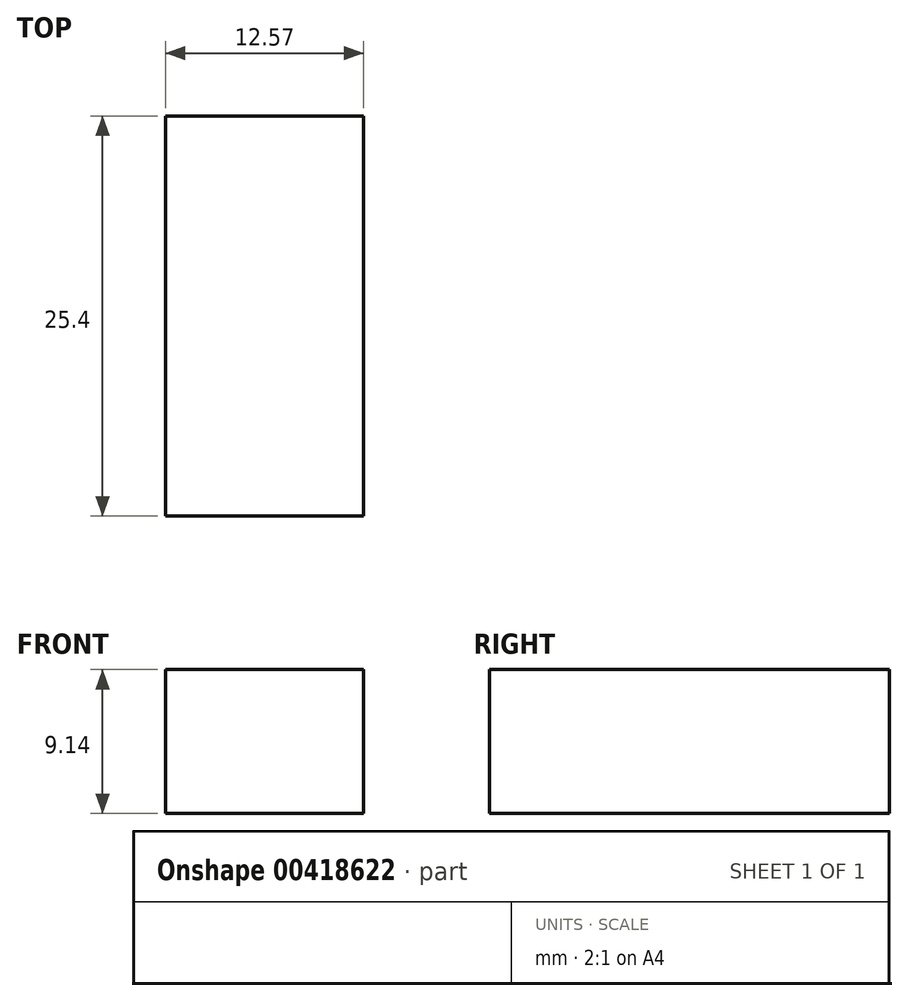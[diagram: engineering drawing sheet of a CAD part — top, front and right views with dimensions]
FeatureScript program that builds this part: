
annotation { "Feature Type Name" : "Feature", "Feature Type Description" : "" }
export const myFeature = defineFeature(function(context is Context, id is Id, definition is map)
    precondition{}
    {
        {
            var Q0;
            Q0=qCreatedBy(makeId("Front.planeOp"),FACE);
            var sketch = newSketch(context, id + "F0", { "sketchPlane" : qUnion([Q0])});
            skLineSegment(sketch, "E0.bottom", {"start": v(0, 0) * mm, "end": v(12.57, 0) * mm});
            skLineSegment(sketch, "E0.top", {"start": v(0, 9.14) * mm, "end": v(12.57, 9.14) * mm});
            skLineSegment(sketch, "E0.left", {"start": v(0, 0) * mm, "end": v(0, 9.14) * mm});
            skLineSegment(sketch, "E0.right", {"start": v(12.57, 0) * mm, "end": v(12.57, 9.14) * mm});
            skSolve(sketch);
        }
        {
            var Q0;
            Q0 = qSketchRegion(id + "F0", true);
            extrude(context, id + "F1", {"entities" : qUnion([Q0]), "depth" : 25.4 * mm});
        }
    });
